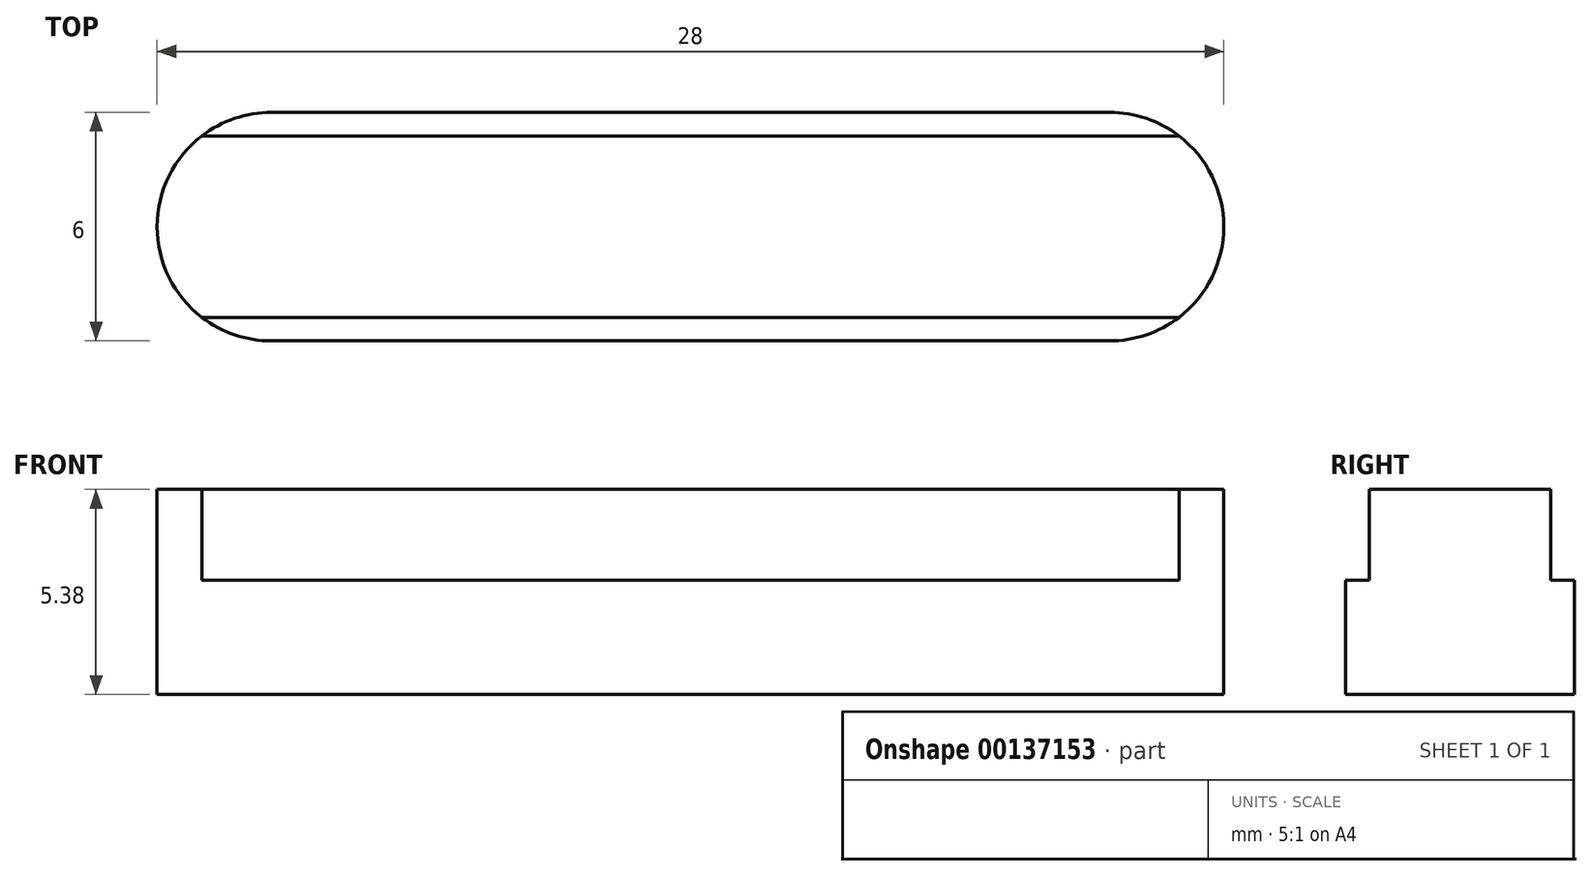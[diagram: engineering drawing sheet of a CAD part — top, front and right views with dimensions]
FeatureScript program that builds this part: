
annotation { "Feature Type Name" : "Feature", "Feature Type Description" : "" }
export const myFeature = defineFeature(function(context is Context, id is Id, definition is map)
    precondition{}
    {
        {
            var Q0;
            Q0=qCreatedBy(makeId("Right.planeOp"),FACE);
            var sketch = newSketch(context, id + "F0", { "sketchPlane" : qUnion([Q0])});
            skLineSegment(sketch, "E0.bottom", {"start": v(2.38, 2.38) * mm, "end": v(-2.38, 2.38) * mm});
            skLineSegment(sketch, "E0.left", {"start": v(2.38, 2.38) * mm, "end": v(2.38, 0) * mm});
            skLineSegment(sketch, "E0.right", {"start": v(-2.38, 2.38) * mm, "end": v(-2.38, 0) * mm});
            skPoint(sketch, "E0.middle", {"position": v(0, 0) * mm});
            skLineSegment(sketch, "E1.top", {"start": v(3, -3) * mm, "end": v(-3, -3) * mm});
            skLineSegment(sketch, "E1.left", {"start": v(3, 0) * mm, "end": v(3, -3) * mm});
            skLineSegment(sketch, "E1.right", {"start": v(-3, 0) * mm, "end": v(-3, -3) * mm});
            skLineSegment(sketch, "E2", {"start": v(-2.38, 0) * mm, "end": v(-3, 0) * mm});
            skLineSegment(sketch, "E3", {"start": v(2.38, 0) * mm, "end": v(3, 0) * mm});
            skLineSegment(sketch, "E4", {"start": v(0, 0) * mm, "end": v(0, 2.38) * mm, "construction": true});
            skLineSegment(sketch, "E5", {"start": v(0, 2.38) * mm, "end": v(2.38, 0) * mm, "construction": true});
            skLineSegment(sketch, "E6", {"start": v(0, 0) * mm, "end": v(2.38, 2.38) * mm, "construction": true});
            skLineSegment(sketch, "E7", {"start": v(0, 0) * mm, "end": v(0, -3) * mm, "construction": true});
            skLineSegment(sketch, "E8", {"start": v(0, -3) * mm, "end": v(3, 0) * mm, "construction": true});
            skLineSegment(sketch, "E9", {"start": v(3, -3) * mm, "end": v(0, 0) * mm, "construction": true});
            skSolve(sketch);
        }
        {
            var Q0;
            Q0=qCreatedBy(makeId("Top.planeOp"),FACE);
            var sketch = newSketch(context, id + "F1", { "sketchPlane" : qUnion([Q0])});
            skLineSegment(sketch, "E10", {"start": v(-11, 3) * mm, "end": v(11, 3) * mm, "construction": true});
            skLineSegment(sketch, "E11", {"start": v(11, 3) * mm, "end": v(11, -3) * mm, "construction": true});
            skLineSegment(sketch, "E12", {"start": v(11, -3) * mm, "end": v(-11, -3) * mm, "construction": true});
            skLineSegment(sketch, "E13", {"start": v(-11, -3) * mm, "end": v(-11, 3) * mm, "construction": true});
            skArc(sketch, "E14", {"start": v(-11, 3) * mm, "mid": v(-14, 0) * mm, "end": v(-11, -3) * mm});
            skArc(sketch, "E15", {"start": v(11, -3) * mm, "mid": v(14, 0) * mm, "end": v(11, 3) * mm});
            skLineSegment(sketch, "E16", {"start": v(-11, 0) * mm, "end": v(0, 0) * mm, "construction": true});
            skLineSegment(sketch, "E17", {"start": v(0, 0) * mm, "end": v(11, 0) * mm, "construction": true});
            skArc(sketch, "E18.0", {"start": v(-11, 9.35) * mm, "mid": v(-20.35, 0) * mm, "end": v(-11, -9.35) * mm});
            skArc(sketch, "E18.2", {"start": v(11, -9.35) * mm, "mid": v(20.35, 0) * mm, "end": v(11, 9.35) * mm});
            skLineSegment(sketch, "E19", {"start": v(-11, -9.35) * mm, "end": v(-11, -3) * mm});
            skLineSegment(sketch, "E20", {"start": v(11, -9.35) * mm, "end": v(11, -3) * mm});
            skLineSegment(sketch, "E21", {"start": v(11, 3) * mm, "end": v(11, 9.35) * mm});
            skLineSegment(sketch, "E22", {"start": v(-11, 3) * mm, "end": v(-11, 9.35) * mm});
            skSolve(sketch);
        }
        {
            var Q0;
            Q0 = qSketchRegion(id + "F0", true);
            extrude(context, id + "F2", {"entities" : qUnion([Q0]), "endBound" : BoundingType.SYMMETRIC, "depth" : 30 * mm});
        }
        {
            var Q0;
            Q0 = qSketchRegion(id + "F1", true);
            extrude(context, id + "F3", {"entities" : qUnion([Q0]), "operationType" : NewBodyOperationType.REMOVE, "endBound" : BoundingType.SYMMETRIC, "oppositeDirection" : true, "depth" : 6 * mm});
        }
    });
